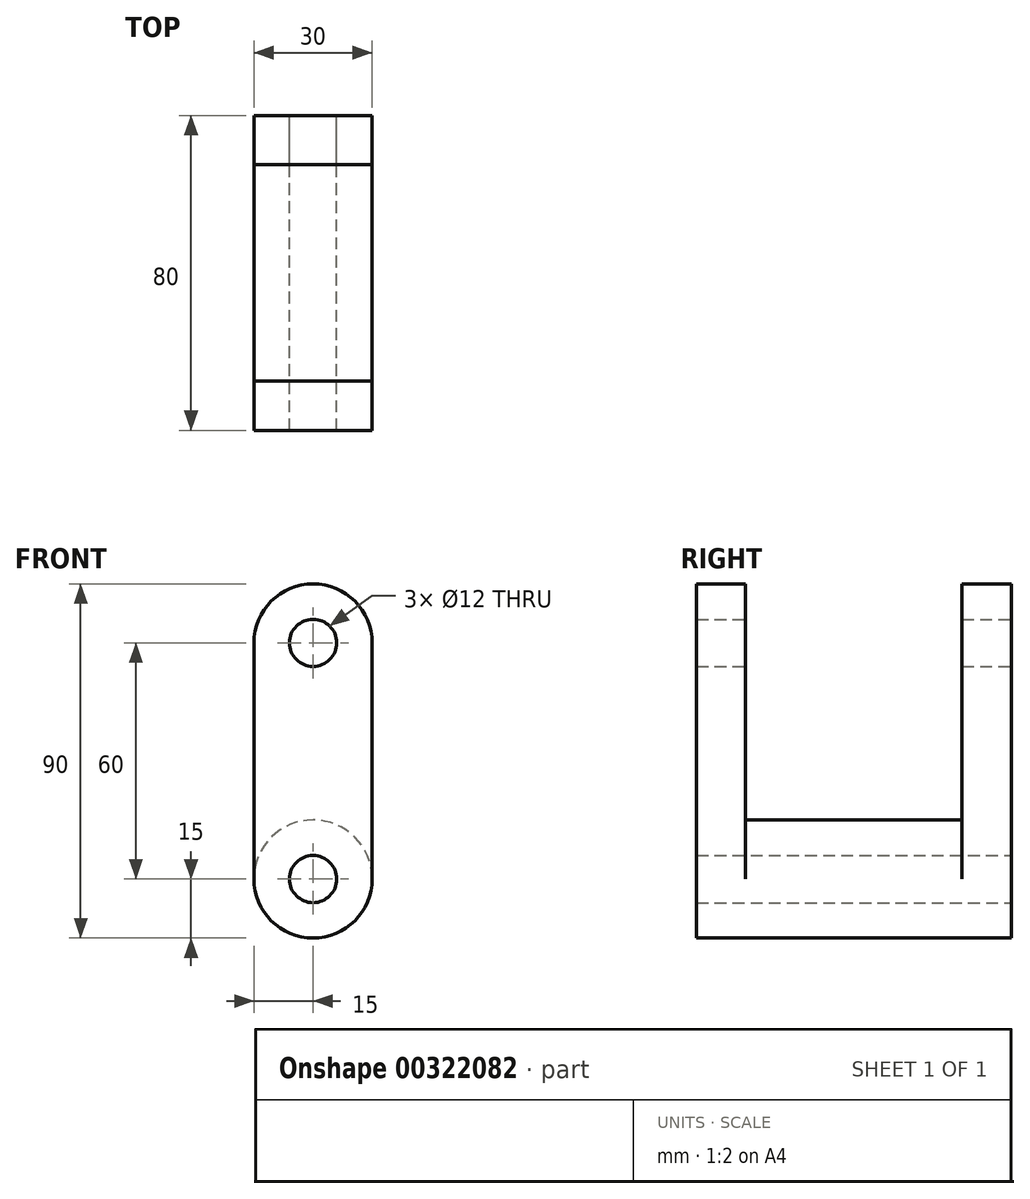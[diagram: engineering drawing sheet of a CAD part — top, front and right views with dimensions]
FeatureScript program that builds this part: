
annotation { "Feature Type Name" : "Feature", "Feature Type Description" : "" }
export const myFeature = defineFeature(function(context is Context, id is Id, definition is map)
    precondition{}
    {
        {
            var Q0;
            Q0=qCreatedBy(makeId("Front.planeOp"),FACE);
            var sketch = newSketch(context, id + "F0", { "sketchPlane" : qUnion([Q0])});
            skLineSegment(sketch, "E0.bottom", {"start": v(15, 30) * mm, "end": v(-15, 30) * mm});
            skLineSegment(sketch, "E0.top", {"start": v(15, -30) * mm, "end": v(-15, -30) * mm});
            skLineSegment(sketch, "E0.left", {"start": v(15, 30) * mm, "end": v(15, -30) * mm});
            skLineSegment(sketch, "E0.right", {"start": v(-15, 30) * mm, "end": v(-15, -30) * mm});
            skPoint(sketch, "E0.middle", {"position": v(0, 0) * mm});
            skCircle(sketch, "E1", {"center": v(0, 30) * mm, "radius": 15 * mm});
            skCircle(sketch, "E2", {"center": v(0, -30) * mm, "radius": 15 * mm});
            skCircle(sketch, "E3", {"center": v(0, 30) * mm, "radius": 6 * mm});
            skCircle(sketch, "E4", {"center": v(0, -30) * mm, "radius": 6 * mm});
            skSolve(sketch);
        }
        {
            var Q0;
            Q0 = qSketchRegion(id + "F0", true);
            extrude(context, id + "F1", {"entities" : qUnion([Q0]), "endBound" : BoundingType.SYMMETRIC, "depth" : 80 * mm});
        }
        {
            var Q0;
            {var subQ0=sQuery(id+"F0.wireOp",EDGE,"E0.left");Q0=makeQuery(id+"F0.imprint","IMPRINT",FACE,{"disambiguationData":[TD([[makeQuery(id+"F0.imprint","IMPRINT",EDGE,{"derivedFrom":subQ0}),-1.0]])]});}
            var Q1;
            {var subQ1=sQuery(id+"F0.wireOp",EDGE,"E0.bottom");var subQ3=sQuery(id+"F0.wireOp",EDGE,"E3");var subQ4=makeQuery(id+"F0.imprint","INTERSECT",VERTEX,{"disambiguationData":[OD(0.0)],"derivedFrom":[subQ1,subQ3]});Q1=makeQuery(id+"F0.imprint","IMPRINT",FACE,{"disambiguationData":[TD([[makeQuery(id+"F0.imprint","IMPRINT",EDGE,{"disambiguationData":[TD([[subQ4,-1.0]])],"derivedFrom":subQ3}),-1.0]])]});}
            var Q2;
            {var subQ1=sQuery(id+"F0.wireOp",EDGE,"E0.bottom");var subQ3=sQuery(id+"F0.wireOp",EDGE,"E3");var subQ4=makeQuery(id+"F0.imprint","INTERSECT",VERTEX,{"disambiguationData":[OD(0.0)],"derivedFrom":[subQ1,subQ3]});Q2=makeQuery(id+"F0.imprint","IMPRINT",FACE,{"disambiguationData":[TD([[makeQuery(id+"F0.imprint","IMPRINT",EDGE,{"disambiguationData":[TD([[subQ4,1.0]])],"derivedFrom":subQ3}),-1.0]])]});}
            extrude(context, id + "F2", {"entities" : qUnion([Q0, Q1, Q2]), "operationType" : NewBodyOperationType.REMOVE, "endBound" : BoundingType.SYMMETRIC, "depth" : 55 * mm});
        }
    });
